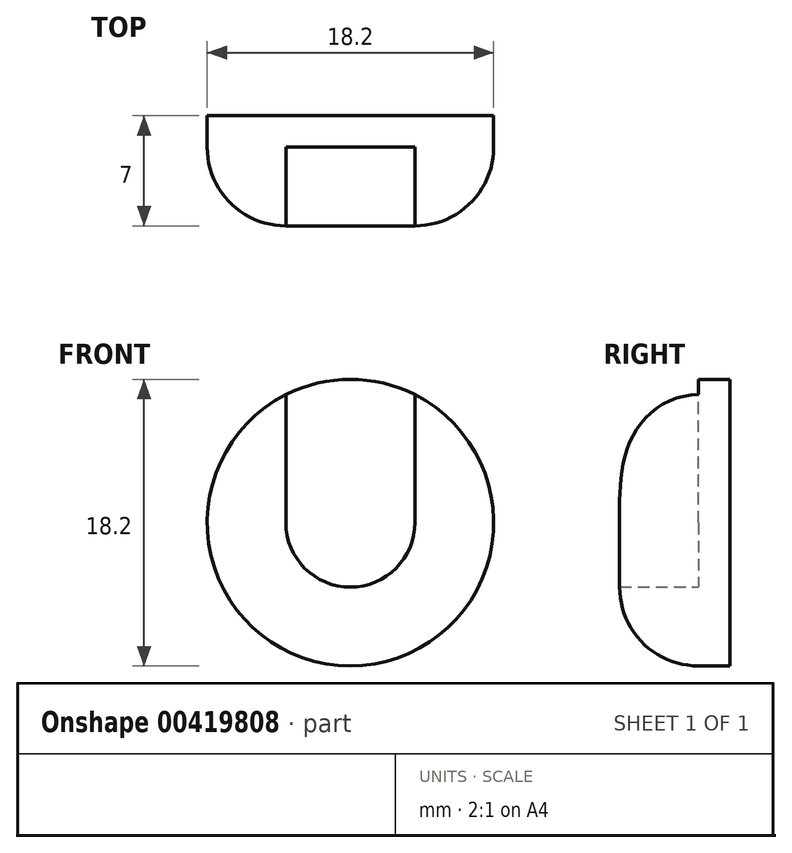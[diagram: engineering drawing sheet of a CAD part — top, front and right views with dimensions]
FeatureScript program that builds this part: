
annotation { "Feature Type Name" : "Feature", "Feature Type Description" : "" }
export const myFeature = defineFeature(function(context is Context, id is Id, definition is map)
    precondition{}
    {
        {
            var Q0;
            Q0=qCreatedBy(makeId("Front.planeOp"),FACE);
            var sketch = newSketch(context, id + "F0", { "sketchPlane" : qUnion([Q0])});
            skCircle(sketch, "E0", {"center": v(0, 0) * mm, "radius": 9.1 * mm});
            skArc(sketch, "E1", {"start": v(-4.1, 0) * mm, "mid": v(0, -4.1) * mm, "end": v(4.1, 0) * mm});
            skLineSegment(sketch, "E2", {"start": v(-4.1, 0) * mm, "end": v(-4.1, 8.12) * mm});
            skLineSegment(sketch, "E3", {"start": v(4.1, 0) * mm, "end": v(4.1, 8.12) * mm});
            skLineSegment(sketch, "E4", {"start": v(-4.1, 0) * mm, "end": v(4.1, 0) * mm, "construction": true});
            skSolve(sketch);
        }
        {
            var Q0;
            Q0=makeQuery(id+"F0.imprint","IMPRINT",FACE,{"disambiguationData":[TD([[makeQuery(id+"F0.imprint","IMPRINT",EDGE,{"derivedFrom":sQuery(id+"F0.wireOp",EDGE,"E1")}),-1.0]])]});
            var Q1;
            Q1=makeQuery(id+"F0.imprint","IMPRINT",FACE,{"disambiguationData":[TD([[makeQuery(id+"F0.imprint","IMPRINT",EDGE,{"derivedFrom":sQuery(id+"F0.wireOp",EDGE,"E1")}),1.0]])]});
            extrude(context, id + "F1", {"entities" : qUnion([Q0, Q1]), "oppositeDirection" : true, "depth" : 2 * mm});
        }
        {
            var Q0;
            Q0=makeQuery(id+"F0.imprint","IMPRINT",FACE,{"disambiguationData":[TD([[makeQuery(id+"F0.imprint","IMPRINT",EDGE,{"derivedFrom":sQuery(id+"F0.wireOp",EDGE,"E1")}),-1.0]])]});
            extrude(context, id + "F2", {"entities" : qUnion([Q0]), "operationType" : NewBodyOperationType.ADD, "depth" : 5 * mm});
        }
        {
            var Q0;
            Q0=makeQuery(id+"F2.opExtrude","CAP_EDGE",EDGE,{"disambiguationData":[OSD([sQuery(id+"F0.wireOp",EDGE,"E0")])],"isStart":false});
            fillet(context, id + "F3", {"entities" : qUnion([Q0]), "radius" : 5 * mm, "tangentPropagation" : true, "allowEdgeOverflow" : false});
        }
    });
